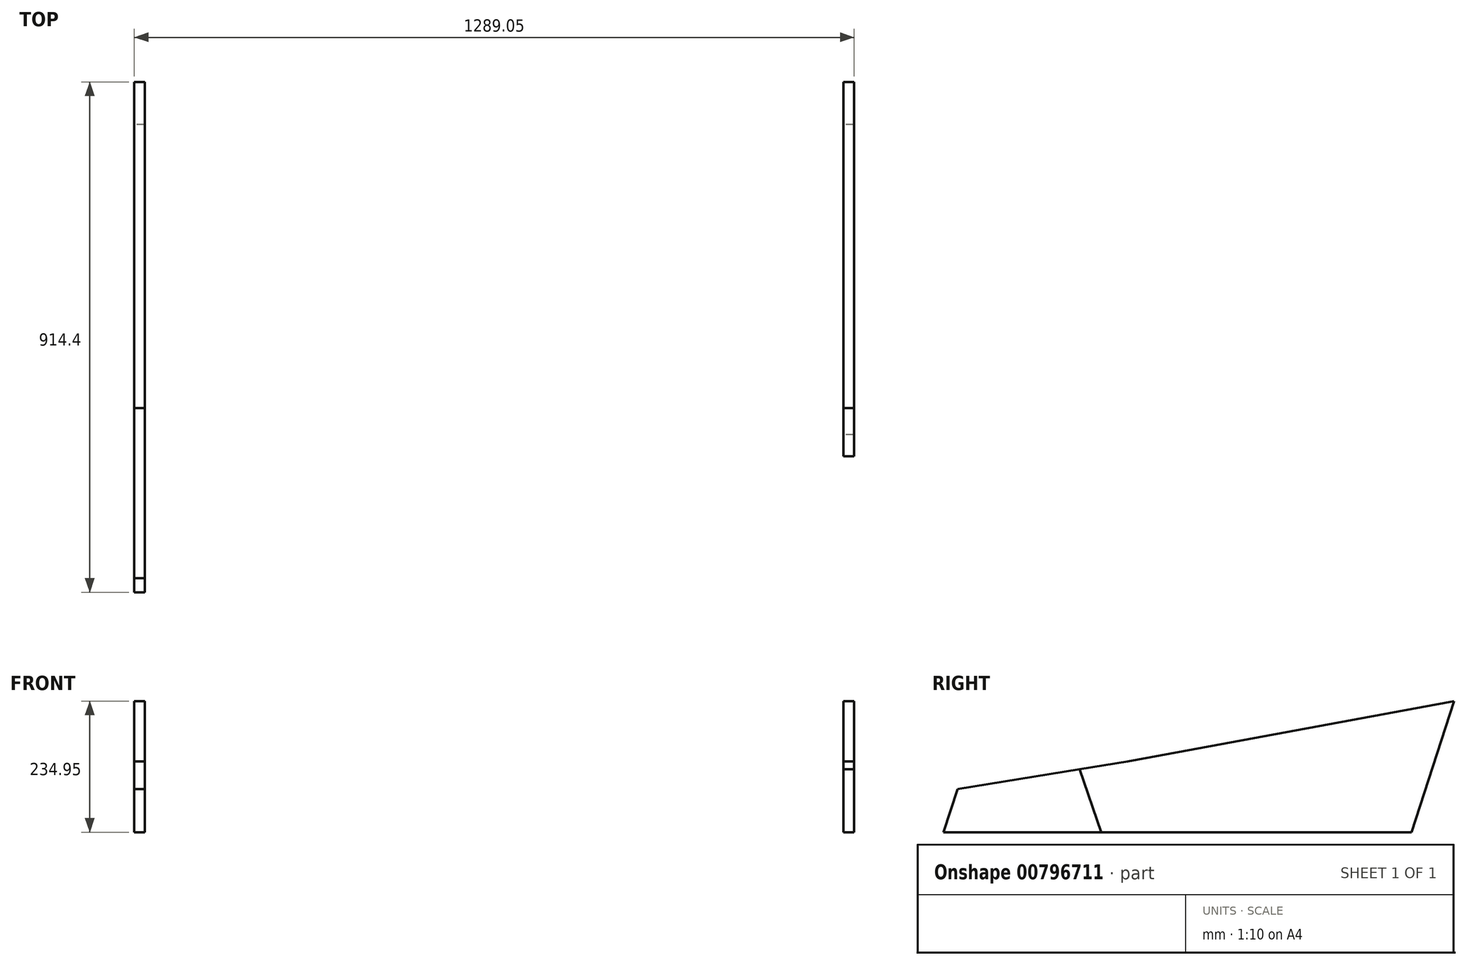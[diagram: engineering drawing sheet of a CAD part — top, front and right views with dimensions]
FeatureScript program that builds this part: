
annotation { "Feature Type Name" : "Feature", "Feature Type Description" : "" }
export const myFeature = defineFeature(function(context is Context, id is Id, definition is map)
    precondition{}
    {
        {
            var Q0;
            Q0=qCreatedBy(makeId("Right.planeOp"),FACE);
            var sketch = newSketch(context, id + "F0", { "sketchPlane" : qUnion([Q0])});
            skLineSegment(sketch, "E0", {"start": v(0, 0) * mm, "end": v(838.2, 0) * mm});
            skLineSegment(sketch, "E1", {"start": v(838.2, 0) * mm, "end": v(914.4, 0) * mm, "construction": true});
            skLineSegment(sketch, "E2", {"start": v(914.4, 0) * mm, "end": v(914.4, 234.95) * mm, "construction": true});
            skLineSegment(sketch, "E3", {"start": v(914.4, 234.95) * mm, "end": v(838.2, 0) * mm});
            skLineSegment(sketch, "E4", {"start": v(914.4, 234.95) * mm, "end": v(330.2, 127) * mm});
            skLineSegment(sketch, "E5", {"start": v(330.2, 127) * mm, "end": v(25.4, 77.18) * mm});
            skLineSegment(sketch, "E6", {"start": v(25.4, 77.18) * mm, "end": v(0, 0) * mm});
            skSolve(sketch);
        }
        {
            var Q0;
            Q0=makeQuery(id+"F0.imprint","IMPRINT",FACE,{"disambiguationData":[TD([[makeQuery(id+"F0.imprint","IMPRINT",EDGE,{"derivedFrom":sQuery(id+"F0.wireOp",EDGE,"E0")}),1.0]])]});
            extrude(context, id + "F1", {"entities" : qUnion([Q0]), "depth" : 19.05 * mm, "offsetDistance" : 25.4 * mm});
        }
        {
            var Q0;
            Q0=qCreatedBy(makeId("Right.planeOp"),FACE);
            var sketch = newSketch(context, id + "F2", { "sketchPlane" : qUnion([Q0])});
            skLineSegment(sketch, "E7.0", {"start": v(914.4, 234.95) * mm, "end": v(838.2, 0) * mm});
            skLineSegment(sketch, "E8", {"start": v(241.3, 0) * mm, "end": v(241.3, 238.5) * mm, "construction": true});
            skLineSegment(sketch, "E9", {"start": v(282.58, 0) * mm, "end": v(282.58, 238.5) * mm, "construction": true});
            skLineSegment(sketch, "E10.0", {"start": v(914.4, 234.95) * mm, "end": v(330.2, 127) * mm});
            skLineSegment(sketch, "E10.1", {"start": v(330.2, 127) * mm, "end": v(241.3, 112.47) * mm});
            skLineSegment(sketch, "E11", {"start": v(241.3, 119.25) * mm, "end": v(282.58, 0) * mm});
            skLineSegment(sketch, "E12", {"start": v(282.58, 0) * mm, "end": v(838.2, 0) * mm});
            skPoint(sketch, "E13.orphan", {"position": v(25.4, 77.18) * mm});
            skSolve(sketch);
        }
        {
            var Q0;
            Q0 = qSketchRegion(id + "F2", true);
            extrude(context, id + "F3", {"entities" : qUnion([Q0]), "depth" : 19.05 * mm, "offsetDistance" : 25.4 * mm});
        }
        {
            var Q0;
            Q0=makeQuery(id+"F3.opExtrude","CAP_FACE",FACE,{"disambiguationData":[OSD([sQuery(id+"F2.wireOp",EDGE,"cc40d755-8581-44e9-a3b7-a1efd18522be.0"),sQuery(id+"F2.wireOp",EDGE,"E7.0"),sQuery(id+"F2.wireOp",EDGE,"71H41THr-Xm2y-CzNQ-JKjM-C5g9EHNxDaZa"),sQuery(id+"F2.wireOp",EDGE,"ax74eQ3t-9lHB-FRBj-idfx-suLznMFMN7Pp"),sQuery(id+"F2.wireOp",EDGE,"IpQF0oPB-0DTS-wWoP-okdo-rtG0zeAvzljT")])],"isStart":false});
            var sketch = newSketch(context, id + "F4", { "sketchPlane" : qUnion([Q0])});
            skLineSegment(sketch, "E14", {"start": v(282.58, 0) * mm, "end": v(25.04, 744.1) * mm});
            skPoint(sketch, "E15.endSnap0", {"position": v(153.8, 372.05) * mm});
            skLineSegment(sketch, "E16", {"start": v(119.11, 744.1) * mm, "end": v(376.65, 0) * mm});
            skLineSegment(sketch, "E17", {"start": v(376.65, 0) * mm, "end": v(282.58, 0) * mm});
            skLineSegment(sketch, "E18", {"start": v(25.04, 744.1) * mm, "end": v(119.11, 744.1) * mm});
            skPoint(sketch, "E19.orphan", {"position": v(153.8, 643.85) * mm});
            skSolve(sketch);
        }
        {
            var Q0;
            Q0=makeQuery(id+"F1.opExtrude","SWEPT_BODY",BODY,{"disambiguationData":[OSD([sQuery(id+"F0.wireOp",EDGE,"E0"),sQuery(id+"F0.wireOp",EDGE,"E3"),sQuery(id+"F0.wireOp",EDGE,"E4"),sQuery(id+"F0.wireOp",EDGE,"E5"),sQuery(id+"F0.wireOp",EDGE,"E6")])]});
            transform(context, id + "F5", {"entities" : qUnion([Q0]), "transformType" : TransformType.TRANSLATION_3D, "dx" : -1270 * mm, "dy" : 0 * mm, "dz" : 0 * mm, "makeCopy" : false});
        }
    });
